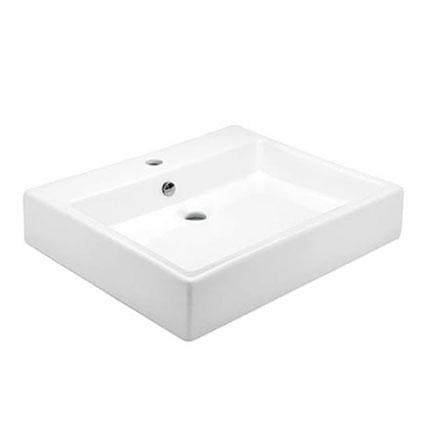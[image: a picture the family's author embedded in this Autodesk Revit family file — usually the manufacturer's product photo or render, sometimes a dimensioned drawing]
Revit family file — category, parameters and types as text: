
# Revit family: LV LUCERNA1_RFA
name_source: partatom
category: Aparatos sanitarios
revit_build: Autodesk Revit 2016 (Build: 20150220_1215(x64)
units: mm (PartAtom-declared; Revit-internal decimal feet)

## family parameters
Compartido = No
Corte con vacíos al cargar = No
Cota de conector redondo = Diámetro de uso
Número OmniClass = 23.45.00.00
Punto de cálculo de habitación = No
Se basa en plano de trabajo = No
Siempre vertical = Sí
Tipo de pieza = Normal
Título OmniClass = Sanitary, Laundry, and Cleaning Equipment

## types (1)
- LV LUCERNA1
    Comentarios de tipo = SANIVEX
    Data Sheet = https://www.helvex.com.mx
    Descripción = Override Sink with Drilling and Overflow
    Fabricante = HELVEX
    Features = Perfect Assembly; Uniformity
    High Gloss Ceramic = High Gloss Ceramic
    Imagen de tipo = LV LUCERNA1.jpg
    Instructive = https://www.helvex.com.mx
    Modelo = LV LUCERNA1
    Total Height = 5"
    Total Length = 18"
    Total Width = 22"
    URL = https://www.helvex.com.mx

## geometry (parser evidence)
native form markers: Sweep x3
no freeform markers — native parametric forms only
